# Revit family: Kabelrinne SKS-SKS 810 FT,FS,A2,A4
name_source: partatom
category: Generic Models
revit_build: Autodesk Revit 2017 (Build: 20160225_1515(x64)
units: mm (PartAtom-declared; Revit-internal decimal feet)

## family parameters
Always vertical = Yes
Can host rebar = No
Cut with Voids When Loaded = No
Part Type = Normal
Room Calculation Point = No
Round Connector Dimension = Use Diameter
Shared = No
Work Plane-Based = No

## types (4) — shared parameters
Cut's number = 2
Cut's number 2 = 60
Cut's number 3 = 59
Cut's number 4 = 3
Cut's space = 50 mm  [stored 0.164042 ft]
Height = 80 mm  [stored 0.262467 ft]
Length = 3000 mm  [stored 9.84252 ft]
Manufacturer = OBO Bettermann
URL = http://www.obo-bettermann.com
Width = 100 mm  [stored 0.328084 ft]
Width 1 = 50 mm  [stored 0.164042 ft]
Width 2 = 50 mm  [stored 0.164042 ft]
Width/2 = 50 mm  [stored 0.164042 ft]

## per-type parameters (varying)
| type | GTIN | Manufacturer Art.No. | Material |
| SKS 810 FT | 4012196061457 | 6058620 | Hot-dip galvanised |
| SKS 810 FS | 4012196061099 | 6058108 | Strip-galvanised |
| SKS 810 A2 | 4012196594979 | 6058760 | Stainless steel, A2 |
| SKS 810 A4 | 4012196661015 | 6058781 | Stainless steel, A4 |

note: column(s) folded — value = type name in every type: Article Type

note: [stored X ft] marks values corroborated as IEEE doubles in the binary element streams (Revit-internal decimal feet)

## geometry (parser evidence)
native form markers: Sweep x1
no freeform markers — native parametric forms only
